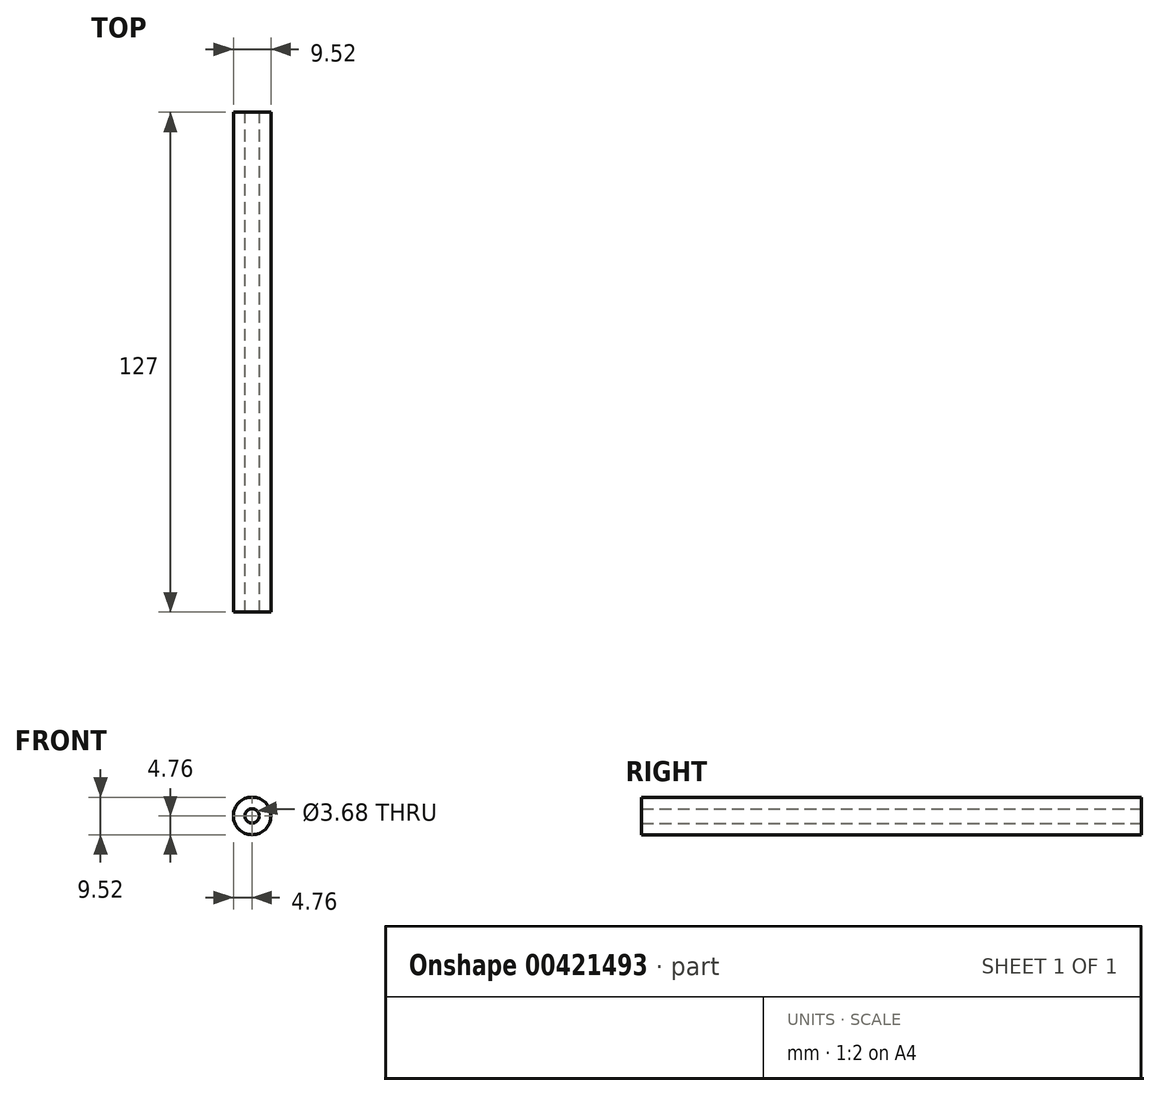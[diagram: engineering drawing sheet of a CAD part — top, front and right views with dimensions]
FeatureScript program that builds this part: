
annotation { "Feature Type Name" : "Feature", "Feature Type Description" : "" }
export const myFeature = defineFeature(function(context is Context, id is Id, definition is map)
    precondition{}
    {
        {
            var Q0;
            Q0=qCreatedBy(makeId("Front.planeOp"),FACE);
            var sketch = newSketch(context, id + "F0", { "sketchPlane" : qUnion([Q0])});
            skCircle(sketch, "E0", {"center": v(0, 0) * mm, "radius": 4.76 * mm});
            skCircle(sketch, "E1", {"center": v(0, 0) * mm, "radius": 1.84 * mm});
            skSolve(sketch);
        }
        {
            var Q0;
            Q0=qSketchRegion(id+"F0",true);
            var Q1;
            Q1=sQuery(id+"F0.wireOp",EDGE,"E0");
            extrude(context, id + "F1", {"entities" : qUnion([Q0]), "surfaceEntities" : qUnion([Q1]), "depth" : 127 * mm});
        }
    });
